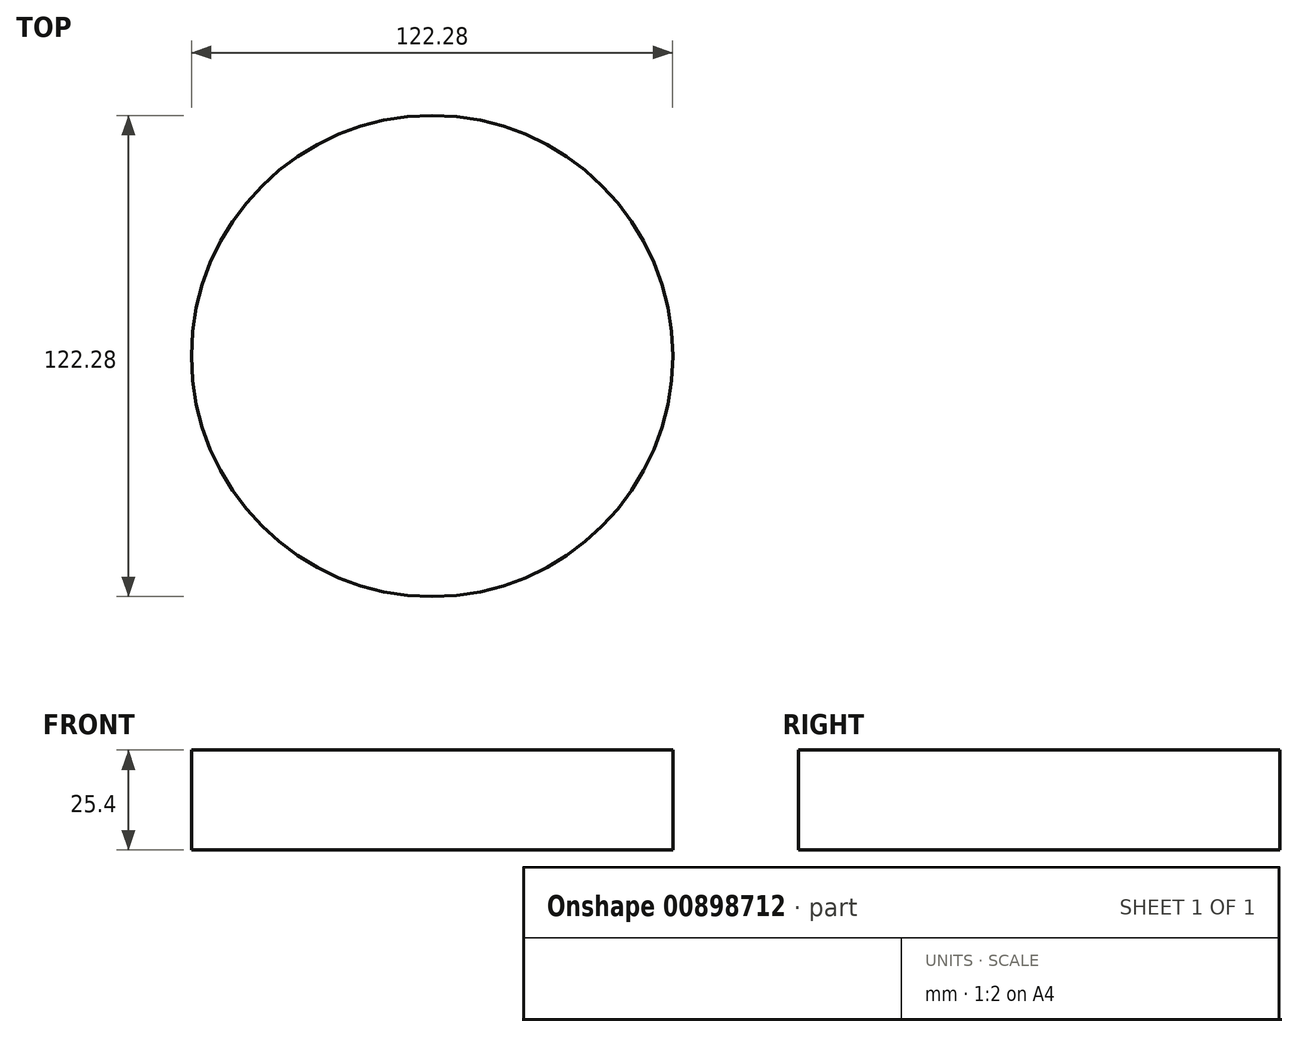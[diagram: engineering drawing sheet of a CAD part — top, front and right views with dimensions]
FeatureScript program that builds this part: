
annotation { "Feature Type Name" : "Feature", "Feature Type Description" : "" }
export const myFeature = defineFeature(function(context is Context, id is Id, definition is map)
    precondition{}
    {
        {
            var Q0;
            Q0=qCreatedBy(makeId("Top.planeOp"),FACE);
            var sketch = newSketch(context, id + "F0", { "sketchPlane" : qUnion([Q0])});
            skCircle(sketch, "E0", {"center": v(0, 0) * mm, "radius": 61.14 * mm});
            skSolve(sketch);
        }
        {
            var Q0;
            Q0=makeQuery(id+"F0.imprint","IMPRINT",FACE,{"disambiguationData":[TD([[makeQuery(id+"F0.imprint","IMPRINT",EDGE,{"derivedFrom":sQuery(id+"F0.wireOp",EDGE,"E0")}),1.0]])]});
            extrude(context, id + "F1", {"entities" : qUnion([Q0]), "depth" : 25.4 * mm, "offsetDistance" : 25.4 * mm});
        }
    });
